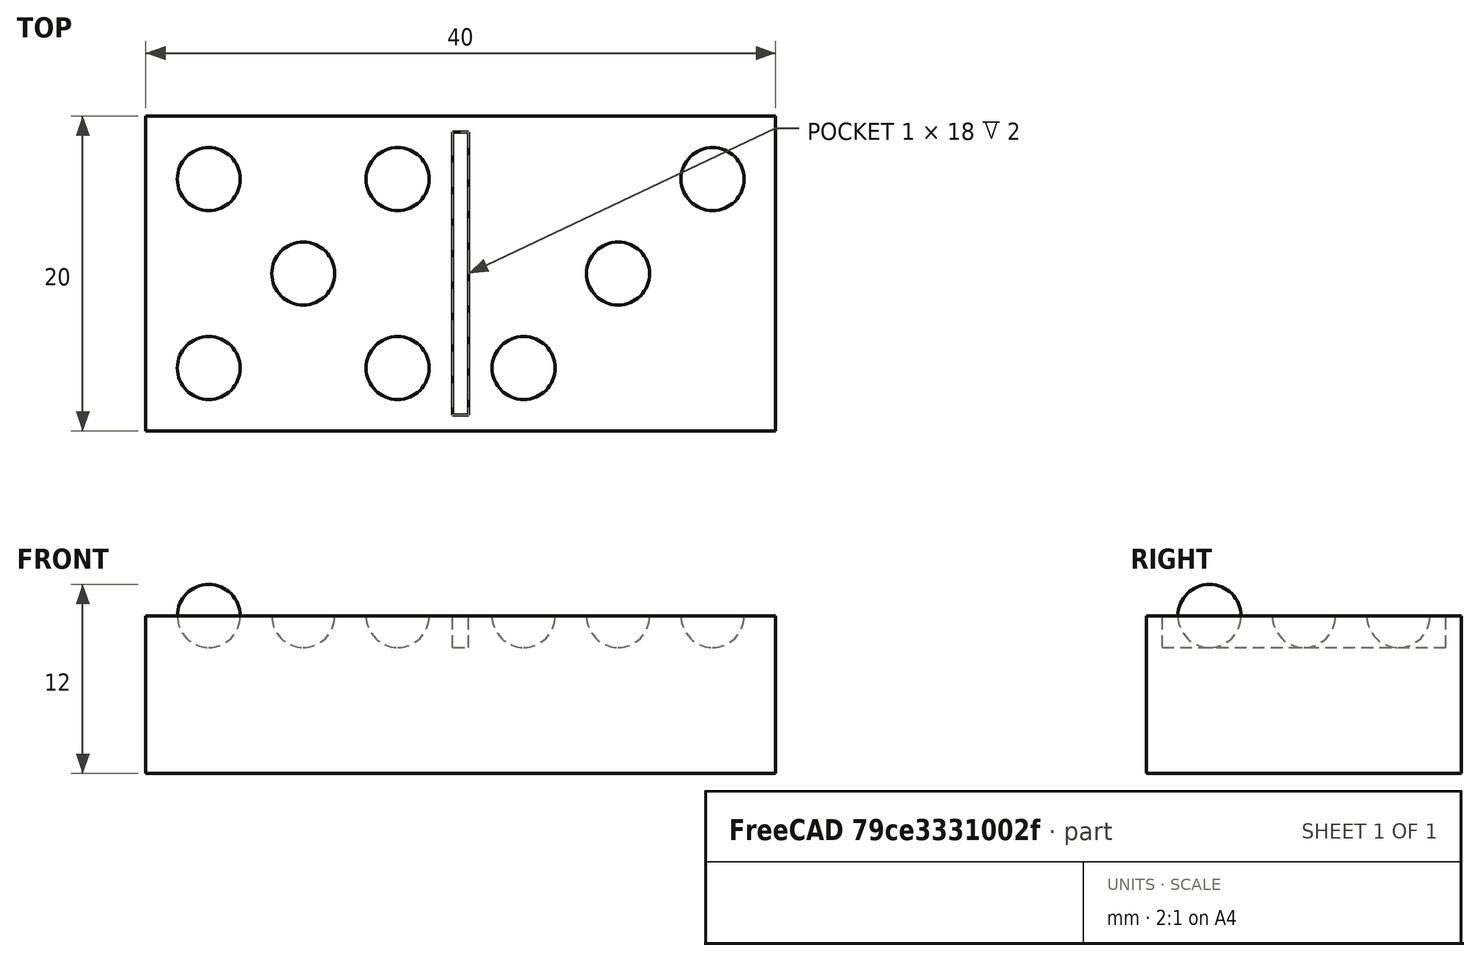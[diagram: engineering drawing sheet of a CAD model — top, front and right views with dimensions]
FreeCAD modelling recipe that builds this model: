
FCSTD DOCUMENT  (FreeCAD 0.21R33694 (Git))
Label: OJT1_T13R03_domino
License: All rights reserved
LicenseURL: https://en.wikipedia.org/wiki/All_rights_reserved
objects: Part::Cut×6, Part::Sphere×5, Part::Box×2, Part::FeaturePython×1
note: 13 computed .brp shape members not serialized (recipe doc carries the construction recipe); baked Part::Feature solids carry a one-line shape summary decoded from their .brp

FEATURE [Part::Box] Box  label="Base domino"
  AttacherType = Attacher::AttachEngine3D
  Height = 10
  Length = 40
  Width = 20
FEATURE [Part::Box] Box001  label="Linia mig"
  AttacherType = Attacher::AttachEngine3D
  Height = 10
  Length = 1
  Placement = pos=(19.5,1,8) rot=(0,0,1;0rad)
  Width = 18
FEATURE [Part::Cut] Cut
  Base = -> Box
  Tool = -> Box001
FEATURE [Part::Sphere] Sphere  label="Esfera"
  Angle1 = -90
  Angle2 = 90
  Angle3 = 360
  AttacherType = Attacher::AttachEngine3D
  Placement = pos=(4,4,10) rot=(0,0,1;0rad)
  Radius = 2
FEATURE [Part::FeaturePython] Array  # Draft array (typed FeaturePython)
  AlwaysSyncPlacement = false
  Angle = 360
  ArrayType = 0
  Axis = (0,0,1)
  Base = -> Sphere
  Center = (0,0,0)
  Count = 4
  ExpandArray = false
  Fuse = false
  IntervalAxis = (0,0,0)
  IntervalX = (12,0,0)
  IntervalY = (0,12,0)
  IntervalZ = (0,0,100)
  NumberCircles = 3
  NumberPolar = 5
  NumberX = 2
  NumberY = 2
  NumberZ = 1
  PlacementList = 4 placements: [(4,4,10),(4,16,10),(16,4,10),(16,16,10)]
  RadialDistance = 50
  ScaleList = (4) [(1,1,1),(1,1,1),(1,1,1),(1,1,1)]
  Symmetry = 1
  TangentialDistance = 25
FEATURE [Part::Cut] Cut001
  Base = -> Cut
  Tool = -> Array
FEATURE [Part::Sphere] Sphere001  label="Esfera001"
  Angle1 = -90
  Angle2 = 90
  Angle3 = 360
  AttacherType = Attacher::AttachEngine3D
  Placement = pos=(10,10,10) rot=(0,0,1;0rad)
  Radius = 2
FEATURE [Part::Cut] Cut002
  Base = -> Cut001
  Tool = -> Sphere001
FEATURE [Part::Sphere] Sphere002  label="Esfera002"
  Angle1 = -90
  Angle2 = 90
  Angle3 = 360
  AttacherType = Attacher::AttachEngine3D
  Placement = pos=(24,4,10) rot=(0,0,1;0rad)
  Radius = 2
FEATURE [Part::Cut] Cut003
  Base = -> Cut002
  Tool = -> Sphere002
FEATURE [Part::Sphere] Sphere003  label="Esfera003"
  Angle1 = -90
  Angle2 = 90
  Angle3 = 360
  AttacherType = Attacher::AttachEngine3D
  Placement = pos=(30,10,10) rot=(0,0,1;0rad)
  Radius = 2
FEATURE [Part::Cut] Cut004
  Base = -> Cut003
  Tool = -> Sphere003
FEATURE [Part::Sphere] Sphere004  label="Esfera004"
  Angle1 = -90
  Angle2 = 90
  Angle3 = 360
  AttacherType = Attacher::AttachEngine3D
  Placement = pos=(36,16,10) rot=(0,0,1;0rad)
  Radius = 2
FEATURE [Part::Cut] Cut005
  Base = -> Cut004
  Tool = -> Sphere004
